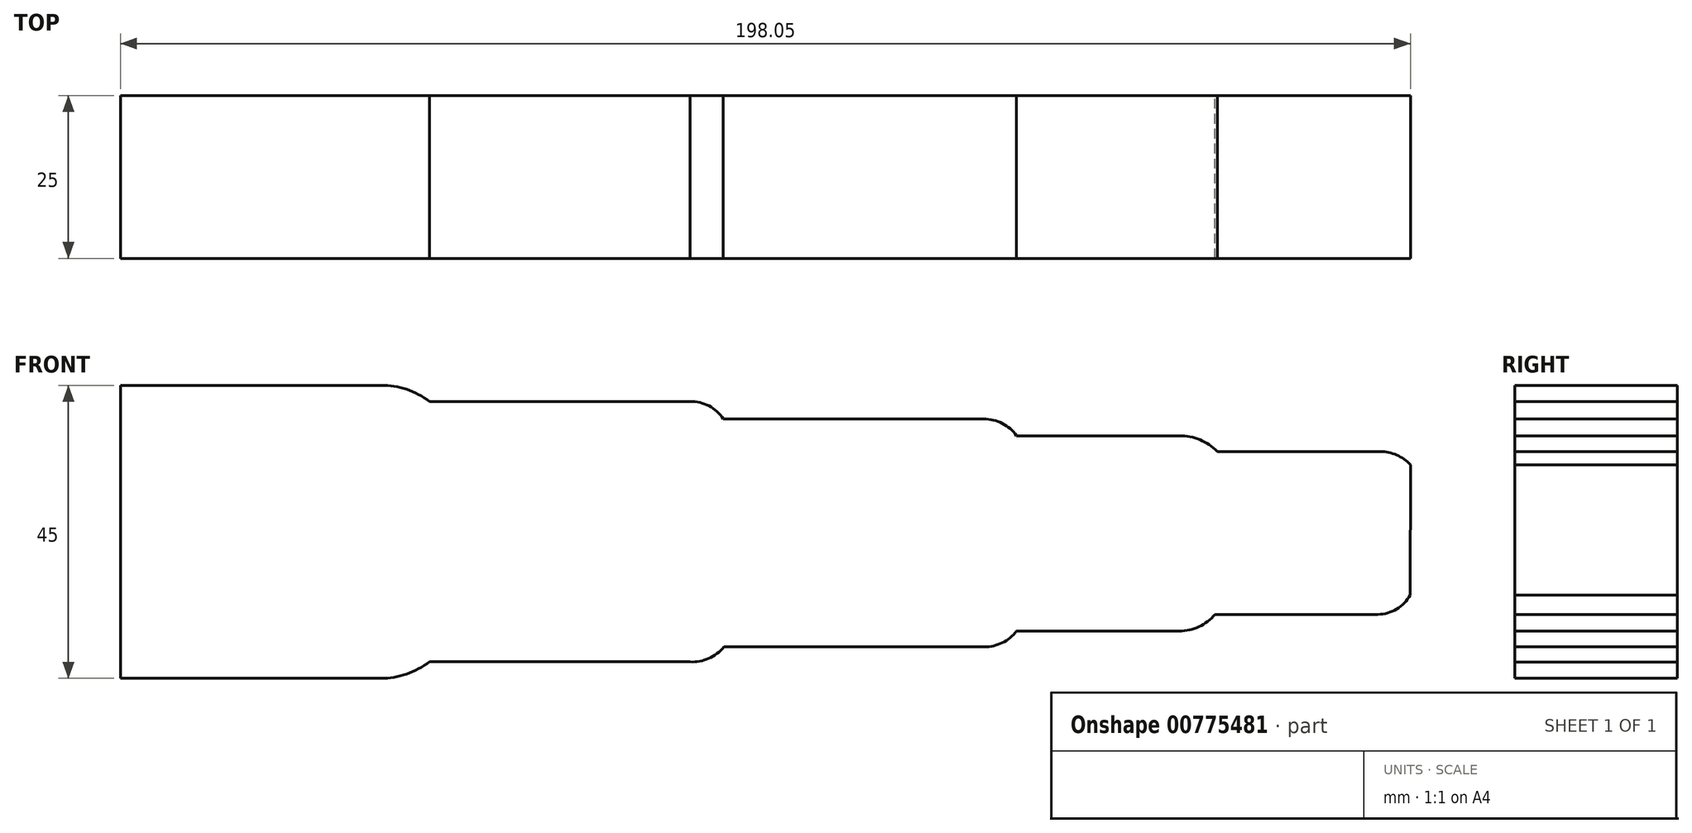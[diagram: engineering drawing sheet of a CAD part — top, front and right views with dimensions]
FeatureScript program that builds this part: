
annotation { "Feature Type Name" : "Feature", "Feature Type Description" : "" }
export const myFeature = defineFeature(function(context is Context, id is Id, definition is map)
    precondition{}
    {
        {
            var Q0;
            Q0=qCreatedBy(makeId("Front.planeOp"),FACE);
            var sketch = newSketch(context, id + "F0", { "sketchPlane" : qUnion([Q0])});
            skLineSegment(sketch, "E0", {"start": v(-87.31, 23.35) * mm, "end": v(-87.31, -21.65) * mm});
            skLineSegment(sketch, "E1", {"start": v(-47.31, -21.65) * mm, "end": v(-87.31, -21.65) * mm});
            skLineSegment(sketch, "E2", {"start": v(-87.31, 23.35) * mm, "end": v(-47.31, 23.35) * mm});
            skArc(sketch, "E3", {"start": v(-39.87, 20.88) * mm, "mid": v(-43.4, 22.72) * mm, "end": v(-47.31, 23.35) * mm});
            skArc(sketch, "E4", {"start": v(-47.31, -21.65) * mm, "mid": v(-43.39, -21) * mm, "end": v(-39.87, -19.12) * mm});
            skLineSegment(sketch, "E5", {"start": v(-39.87, 20.88) * mm, "end": v(0.13, 20.88) * mm});
            skLineSegment(sketch, "E6", {"start": v(-39.87, -19.12) * mm, "end": v(0.13, -19.12) * mm});
            skArc(sketch, "E7", {"start": v(5.24, 18.18) * mm, "mid": v(3.03, 20.18) * mm, "end": v(0.13, 20.88) * mm});
            skArc(sketch, "E8", {"start": v(0.13, -19.12) * mm, "mid": v(3, -18.6) * mm, "end": v(5.33, -16.82) * mm});
            skLineSegment(sketch, "E9", {"start": v(5.24, 18.18) * mm, "end": v(45.24, 18.18) * mm});
            skArc(sketch, "E10", {"start": v(50.26, 15.6) * mm, "mid": v(48.06, 17.5) * mm, "end": v(45.24, 18.18) * mm});
            skLineSegment(sketch, "E11", {"start": v(50.26, 15.6) * mm, "end": v(75.26, 15.6) * mm});
            skArc(sketch, "E12", {"start": v(81.07, 13.18) * mm, "mid": v(78.41, 14.98) * mm, "end": v(75.26, 15.6) * mm});
            skLineSegment(sketch, "E13", {"start": v(81.07, 13.18) * mm, "end": v(106.07, 13.18) * mm});
            skArc(sketch, "E14", {"start": v(110.74, 11.15) * mm, "mid": v(108.62, 12.65) * mm, "end": v(106.07, 13.18) * mm});
            skLineSegment(sketch, "E15", {"start": v(5.33, -16.82) * mm, "end": v(45.33, -16.82) * mm});
            skArc(sketch, "E16", {"start": v(45.33, -16.82) * mm, "mid": v(48.08, -16.18) * mm, "end": v(50.26, -14.4) * mm});
            skLineSegment(sketch, "E17", {"start": v(50.26, -14.4) * mm, "end": v(75.26, -14.4) * mm});
            skArc(sketch, "E18", {"start": v(75.26, -14.4) * mm, "mid": v(78.28, -13.72) * mm, "end": v(80.73, -11.82) * mm});
            skLineSegment(sketch, "E19", {"start": v(80.73, -11.82) * mm, "end": v(105.73, -11.82) * mm});
            skArc(sketch, "E20", {"start": v(105.73, -11.82) * mm, "mid": v(108.62, -11.02) * mm, "end": v(110.69, -8.85) * mm});
            skLineSegment(sketch, "E21", {"start": v(110.69, -8.85) * mm, "end": v(110.74, 11.15) * mm});
            skSolve(sketch);
        }
        {
            var Q0;
            Q0 = qSketchRegion(id + "F0", true);
            extrude(context, id + "F1", {"entities" : qUnion([Q0]), "depth" : 25 * mm, "offsetDistance" : 25 * mm});
        }
    });
